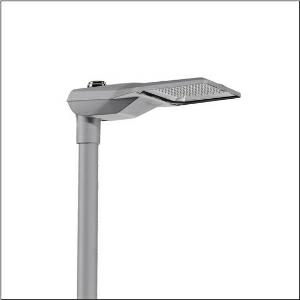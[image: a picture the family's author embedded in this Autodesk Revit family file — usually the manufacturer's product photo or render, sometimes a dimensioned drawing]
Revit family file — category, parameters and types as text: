
# Revit family: streetlight_sl_21_midi___st0_8a_5xe7c37n08mb_215a
name_source: partatom
category: Lighting Fixtures
units: mm (PartAtom-declared; Revit-internal decimal feet)

## family parameters
Cut with Voids When Loaded = No
Host = Face
Light Source = No
Part Type = Normal
Room Calculation Point = No
Round Connector Dimension = Use Diameter
Shared = No

## types (1)
- --- (1 x LED, 18270 lm, 136 W, 3000K)
    Apparent Load = 136 VA
    CIE Flux Codes = 38 75 97 100 100
    Color Rendering = 70
    Color Temperature = 3000K
    Default Elevation = 1800 mm
    Description = Streetlight SL 21 midi, mast luminaire, primary light control with lens, of PMMA, primary optical cover: cover, of toughened safety glass, transparent, light distribution: ST0.8a, light emission: direct distribution, primary light characteristic: asymmetric, installation type: side-entry, LED, 3G 2.5mm², High Power LED, rated luminous flux: 18.270lm, luminous efficacy: 134lm/W, light colour: 730, colour temperature: 3000K, control gear: NEMA (7pin), control: overheat protection, pre-setting: linear dimming characteristic, constant luminous flux control, time-dependent luminous flux control, flexible luminous flux parameterisation, mains connection: 220..240V, AC, 50/60Hz, connection cable pre-assembled, cable length: 12,5m, wiring characteristics: H05VV-F, start of lifetime: 136W, end of service life: 142W, reduction: 61W, luminaire housing, of diecast aluminium (EN AC-44300), powder-coated, SITECO metallic grey (DB 702S), corrosivity category C5 high according to DIN EN ISO 12944, multi-level sealing system, sealing non-destructively replaceable, inclination adjustable: 0°, 5°, 10°, 15°, length: 644mm, width: 335mm, height: 110mm, spigot size: 42mm (side-entry), mounting height: 4..8m, protection rating (complete): IP66, insulation class (complete): insulation class I (protective earthing), certification: CE, ENEC, ENEC+, VDE, impact resistance: IK10, permissible operating ambient temperature for outdoor applications: -40..+50°C, standard-compliant lighting for roads and squares, packaging unit: 1 piece

Light Distribution: ST0.8a
    Height = 111 mm
    Lamp = 1 x LED
    Lamp Light Flux = 18270 lm
    Lamp Power = 136 W
    Lamp count = 1
    Length = 644 mm
    Luminous efficacy = 134 lm/W
    Manufacturer = Siteco
    ModVariant = No
    Model = 5XE7C37N08MB
    Number of Poles = 1
    OnlyDefault = Yes
    Power Factor = 1
    Product Name = Streetlight SL 21 midi | ST0.8a
    Product group = mast luminaire | pylon top
    ProductGroupID = 6100
    Protection Class = Protection class I
    Protection Degree = IP 66
    RLX_Detail_Level = 1
    RLX_Emergency_Light_Flux = 0 lm
    RLX_Emergency_Type = 0
    RLX_Emergency_Type_DB = No
    RlxData = <blob elided: 26561 chars, md5=b37c41f1>
    Socket = socket
    Standby Power = 0 W
    System Light Flux = 18270 lm
    System Power = 136 W
    Type Comments = factory setting: luminous flux: 100 % | dim-lin: 254 | 695 mA
    Type Image = l_1294377.jpg
    URL = http://relux.com
    VarID = @adj_133565
    Voltage = 0 V
    Weight = 0.00 kg
    Width = 336 mm

## geometry (parser evidence)
native form markers: Blend x4, Sweep x12
no freeform markers — native parametric forms only
